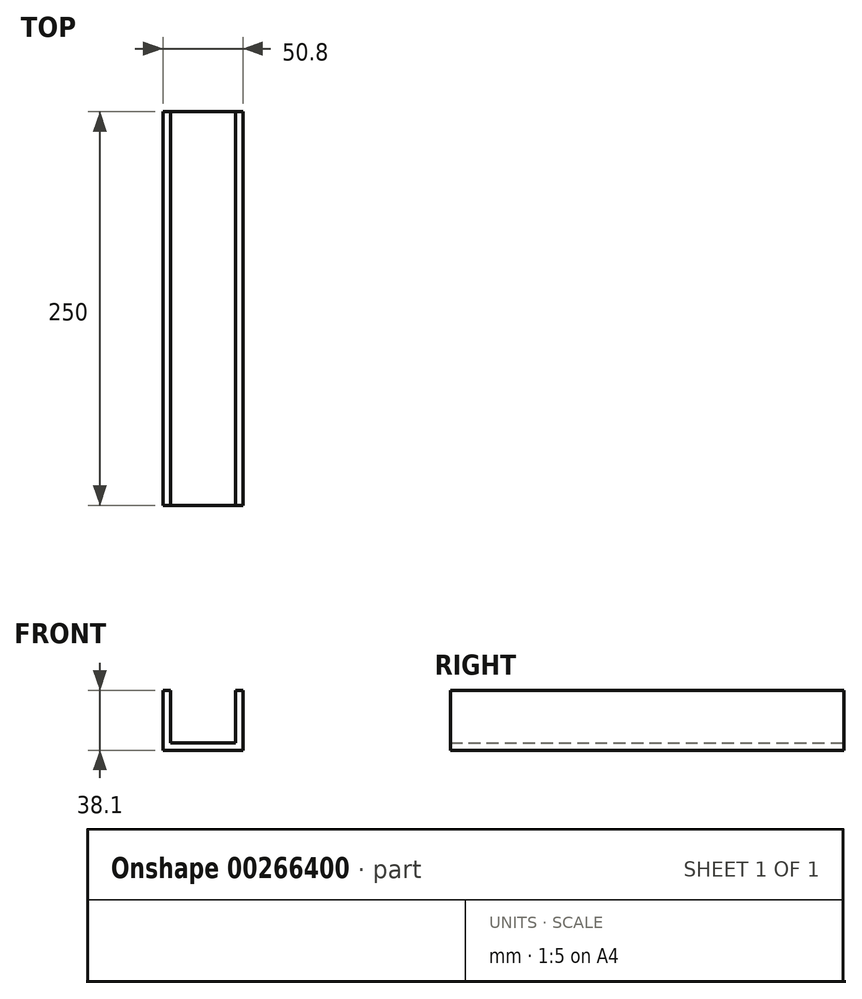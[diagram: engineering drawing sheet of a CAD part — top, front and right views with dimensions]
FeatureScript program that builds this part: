
annotation { "Feature Type Name" : "Feature", "Feature Type Description" : "" }
export const myFeature = defineFeature(function(context is Context, id is Id, definition is map)
    precondition{}
    {
        {
            var Q0;
            Q0=qCreatedBy(makeId("Front.planeOp"),FACE);
            var sketch = newSketch(context, id + "F0", { "sketchPlane" : qUnion([Q0])});
            skLineSegment(sketch, "E0.bottom", {"start": v(25.4, -19.05) * mm, "end": v(-25.4, -19.05) * mm});
            skLineSegment(sketch, "E0.top", {"start": v(25.4, 19.05) * mm, "end": v(-25.4, 19.05) * mm});
            skLineSegment(sketch, "E0.left", {"start": v(25.4, -19.05) * mm, "end": v(25.4, 19.05) * mm});
            skLineSegment(sketch, "E0.right", {"start": v(-25.4, -19.05) * mm, "end": v(-25.4, 19.05) * mm});
            skPoint(sketch, "E0.middle", {"position": v(0, 0) * mm});
            skLineSegment(sketch, "E1", {"start": v(0, -19.05) * mm, "end": v(0, -14.3) * mm, "construction": true});
            skPoint(sketch, "E1.endSnap0", {"position": v(0, -19.05) * mm});
            skLineSegment(sketch, "E2", {"start": v(-25.4, 0) * mm, "end": v(-20.64, 0) * mm, "construction": true});
            skPoint(sketch, "E2.endSnap0", {"position": v(-25.4, 0) * mm});
            skLineSegment(sketch, "E3", {"start": v(-20.64, 0) * mm, "end": v(-20.64, 19.05) * mm});
            skLineSegment(sketch, "E4", {"start": v(-20.64, 0) * mm, "end": v(-20.64, -14.3) * mm});
            skLineSegment(sketch, "E5", {"start": v(-20.64, -14.3) * mm, "end": v(0, -14.3) * mm});
            skLineSegment(sketch, "E6", {"start": v(25.4, 0) * mm, "end": v(20.64, 0) * mm, "construction": true});
            skPoint(sketch, "E6.endSnap0", {"position": v(25.4, 0) * mm});
            skLineSegment(sketch, "E7", {"start": v(20.64, 0) * mm, "end": v(20.64, -14.29) * mm});
            skLineSegment(sketch, "E8", {"start": v(20.64, -14.29) * mm, "end": v(0, -14.3) * mm});
            skLineSegment(sketch, "E9", {"start": v(20.64, 0) * mm, "end": v(20.64, 19.05) * mm});
            skSolve(sketch);
        }
        {
            var Q0;
            Q0=makeQuery(id+"F0.imprint","IMPRINT",FACE,{"disambiguationData":[TD([[makeQuery(id+"F0.imprint","IMPRINT",EDGE,{"derivedFrom":sQuery(id+"F0.wireOp",EDGE,"E0.bottom")}),-1.0]])]});
            extrude(context, id + "F1", {"entities" : qUnion([Q0]), "depth" : 125 * mm, "offsetDistance" : 25 * mm, "hasSecondDirection" : true, "secondDirectionOppositeDirection" : true, "secondDirectionDepth" : 125 * mm});
        }
    });
